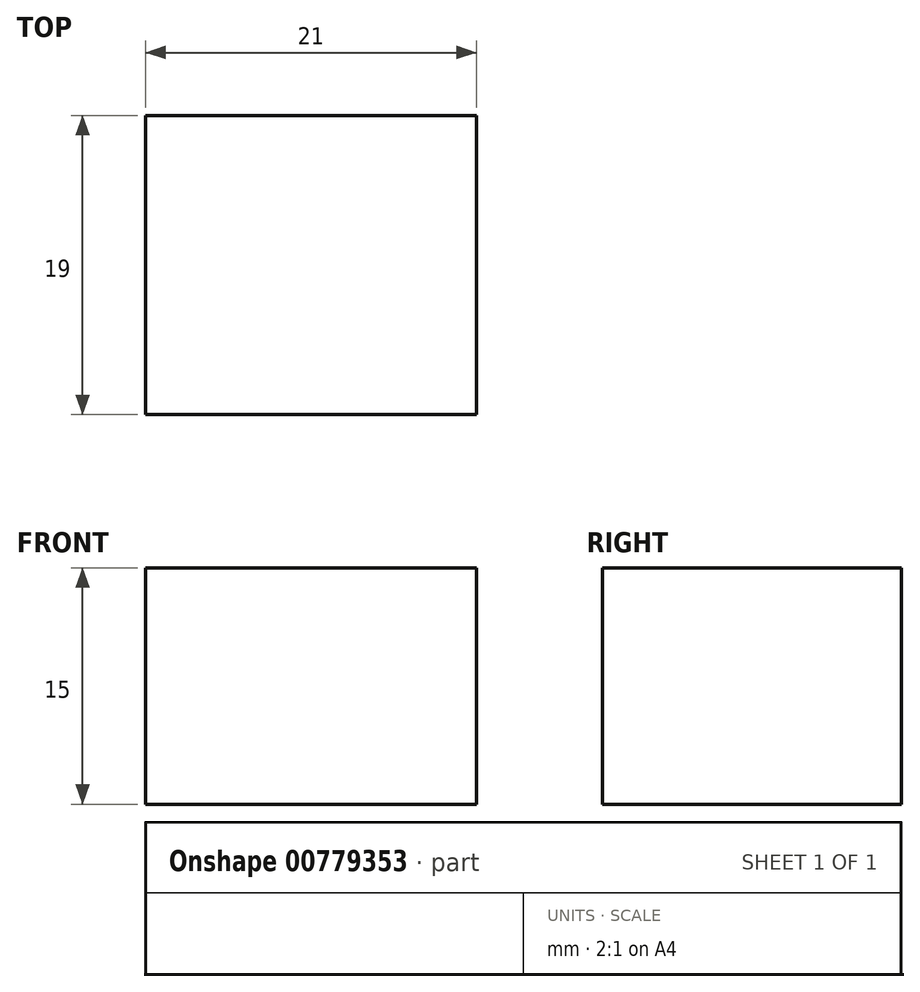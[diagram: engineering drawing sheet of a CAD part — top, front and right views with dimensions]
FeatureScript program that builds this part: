
annotation { "Feature Type Name" : "Feature", "Feature Type Description" : "" }
export const myFeature = defineFeature(function(context is Context, id is Id, definition is map)
    precondition{}
    {
        {
            var Q0;
            Q0=qCreatedBy(makeId("Top.planeOp"),FACE);
            var sketch = newSketch(context, id + "F0", { "sketchPlane" : qUnion([Q0])});
            skLineSegment(sketch, "E0.bottom", {"start": v(0, 0) * mm, "end": v(21, 0) * mm});
            skLineSegment(sketch, "E0.top", {"start": v(0, -19) * mm, "end": v(21, -19) * mm});
            skLineSegment(sketch, "E0.left", {"start": v(0, 0) * mm, "end": v(0, -19) * mm});
            skLineSegment(sketch, "E0.right", {"start": v(21, 0) * mm, "end": v(21, -19) * mm});
            skSolve(sketch);
        }
        {
            var Q0;
            Q0 = qSketchRegion(id + "F0", true);
            extrude(context, id + "F1", {"entities" : qUnion([Q0]), "depth" : 15 * mm, "offsetDistance" : 25 * mm});
        }
    });
